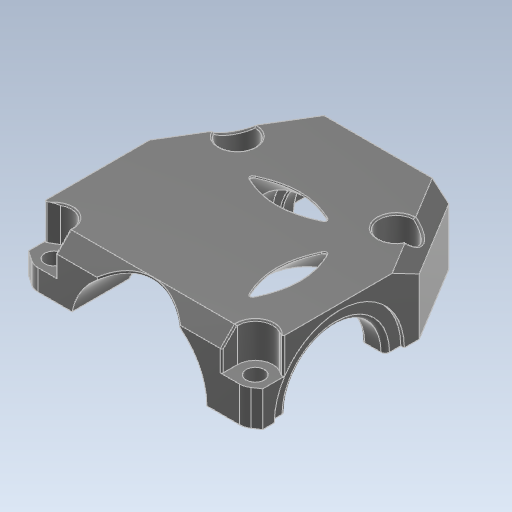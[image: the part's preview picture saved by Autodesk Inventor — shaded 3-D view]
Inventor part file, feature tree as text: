
AUTODESK INVENTOR PART (.ipt)
format: ipt  version: 2024 (Build 280153000, 153)  size: 602,112 bytes
history: native  units: mm
features: other x5, fillet x2, mirror x1, chamfer x1, extrude x1, sketch x1
ambient origin geometry x8: Origin, YZ Plane, XZ Plane, XY Plane, X Axis, Y Axis, Z Axis, Center Point
bodies: Body1 (feature_tree)
feature tree (11):
  other  "_bridseye_sketch.ipt"
  fillet  "フィレット1"  Radius=10.0mm
  mirror  "ミラー1"
  chamfer  "面取り2"  Distance=0.2mm
  extrude  "押し出し2"  Depth=0.1mm
  fillet  "フィレット2"  Radius=5.0mm
  other  "ソリッド16::_bridseye_sketch.ipt"
  other  "TaggingFeature1"
  other  "top_elbowUnit"
  sketch  "スケッチ3"
  other  "ソリッド16"
